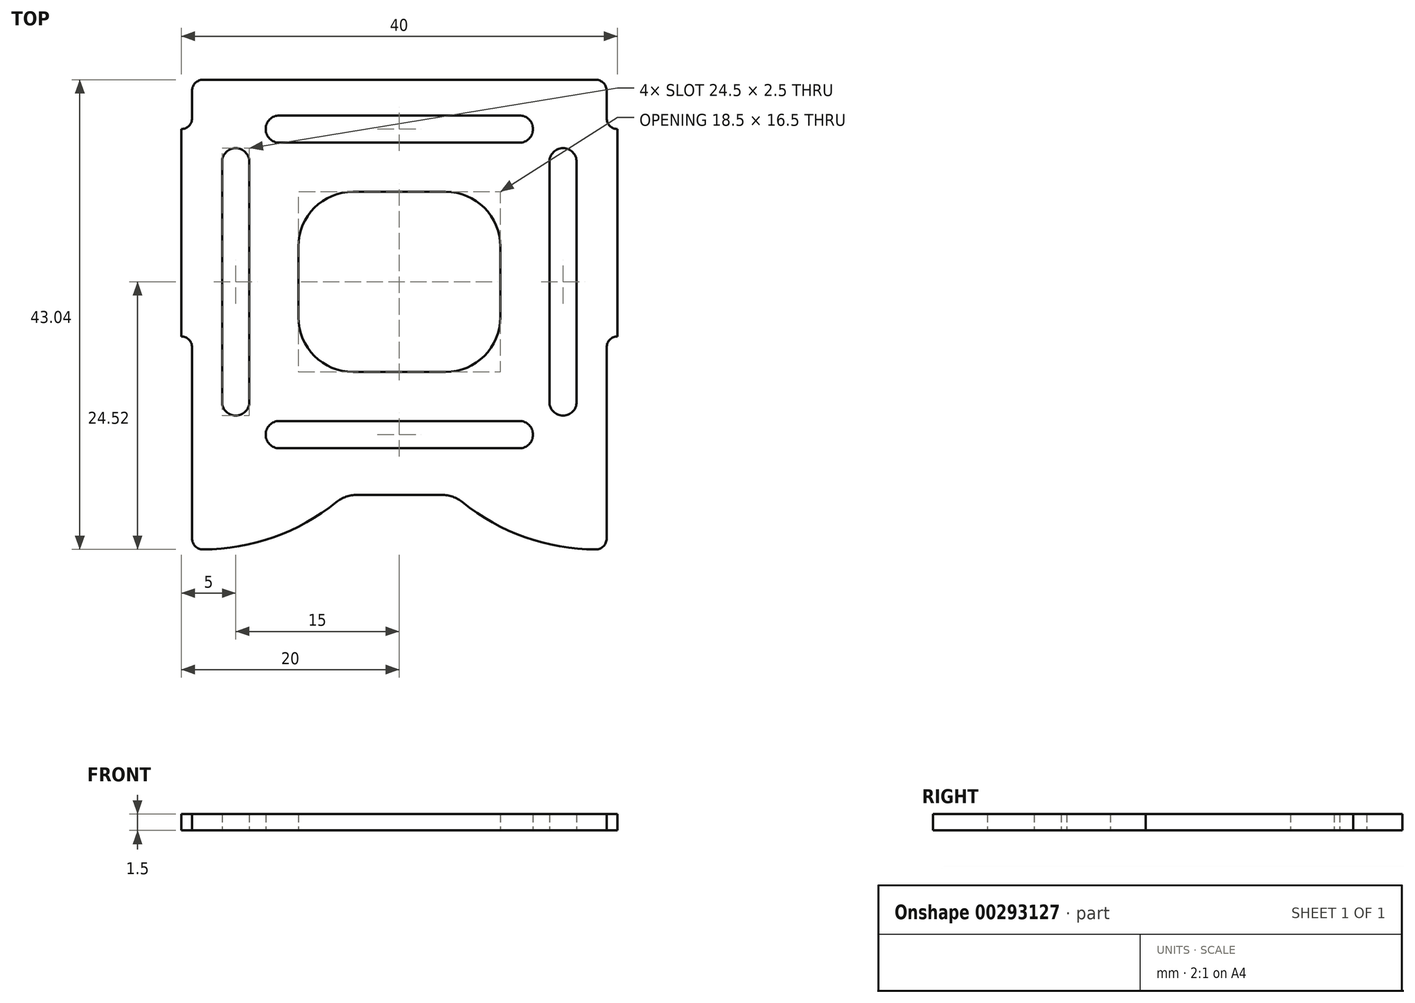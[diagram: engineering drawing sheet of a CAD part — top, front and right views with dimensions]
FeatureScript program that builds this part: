
annotation { "Feature Type Name" : "Feature", "Feature Type Description" : "" }
export const myFeature = defineFeature(function(context is Context, id is Id, definition is map)
    precondition{}
    {
        {
            var Q0;
            Q0=qCreatedBy(makeId("Top.planeOp"),FACE);
            var sketch = newSketch(context, id + "F0", { "sketchPlane" : qUnion([Q0])});
            skArc(sketch, "E0", {"start": v(-20, 17) * mm, "mid": v(-19.3, 17.3) * mm, "end": v(-19, 18) * mm});
            skLineSegment(sketch, "E1", {"start": v(-19, 18) * mm, "end": v(-19, 20.52) * mm});
            skArc(sketch, "E2", {"start": v(-18, 21.52) * mm, "mid": v(-18.7, 21.23) * mm, "end": v(-19, 20.52) * mm});
            skLineSegment(sketch, "E3", {"start": v(-18, 21.52) * mm, "end": v(18, 21.52) * mm});
            skArc(sketch, "E4", {"start": v(19, 20.52) * mm, "mid": v(18.7, 21.23) * mm, "end": v(18, 21.52) * mm});
            skLineSegment(sketch, "E5", {"start": v(19, 20.52) * mm, "end": v(19, 18) * mm});
            skArc(sketch, "E6", {"start": v(19, 18) * mm, "mid": v(19.3, 17.3) * mm, "end": v(20, 17) * mm});
            skLineSegment(sketch, "E7", {"start": v(20, 17) * mm, "end": v(20, -2) * mm});
            skArc(sketch, "E8", {"start": v(20, -2) * mm, "mid": v(19.3, -2.3) * mm, "end": v(19, -3) * mm});
            skLineSegment(sketch, "E9", {"start": v(19, -3) * mm, "end": v(19, -20.52) * mm});
            skArc(sketch, "E10", {"start": v(18, -21.52) * mm, "mid": v(18.7, -21.23) * mm, "end": v(19, -20.52) * mm});
            skArc(sketch, "E11", {"start": v(-19, -20.52) * mm, "mid": v(-18.7, -21.23) * mm, "end": v(-18, -21.52) * mm});
            skLineSegment(sketch, "E12", {"start": v(-19, -20.52) * mm, "end": v(-19, -3) * mm});
            skArc(sketch, "E13", {"start": v(-19, -3) * mm, "mid": v(-19.3, -2.3) * mm, "end": v(-20, -2) * mm});
            skLineSegment(sketch, "E14", {"start": v(-20, -2) * mm, "end": v(-20, 17) * mm});
            skLineSegment(sketch, "E15", {"start": v(-4.25, -5.25) * mm, "end": v(4.25, -5.25) * mm});
            skArc(sketch, "E16", {"start": v(-9.25, -0.25) * mm, "mid": v(-7.79, -3.79) * mm, "end": v(-4.25, -5.25) * mm});
            skLineSegment(sketch, "E17", {"start": v(-9.25, 6.25) * mm, "end": v(-9.25, -0.25) * mm});
            skArc(sketch, "E18", {"start": v(-4.25, 11.25) * mm, "mid": v(-7.79, 9.79) * mm, "end": v(-9.25, 6.25) * mm});
            skLineSegment(sketch, "E19", {"start": v(4.25, 11.25) * mm, "end": v(-4.25, 11.25) * mm});
            skArc(sketch, "E20", {"start": v(9.25, 6.25) * mm, "mid": v(7.79, 9.79) * mm, "end": v(4.25, 11.25) * mm});
            skLineSegment(sketch, "E21", {"start": v(9.25, -0.25) * mm, "end": v(9.25, 6.25) * mm});
            skArc(sketch, "E22", {"start": v(4.25, -5.25) * mm, "mid": v(7.79, -3.79) * mm, "end": v(9.25, -0.25) * mm});
            skLineSegment(sketch, "E23", {"start": v(11, -9.75) * mm, "end": v(-11, -9.75) * mm});
            skArc(sketch, "E24", {"start": v(11, -12.25) * mm, "mid": v(12.25, -11) * mm, "end": v(11, -9.75) * mm});
            skLineSegment(sketch, "E25", {"start": v(-11, -12.25) * mm, "end": v(11, -12.25) * mm});
            skArc(sketch, "E26", {"start": v(-11, -9.75) * mm, "mid": v(-12.25, -11) * mm, "end": v(-11, -12.25) * mm});
            skArc(sketch, "E27", {"start": v(16.25, 14) * mm, "mid": v(15, 15.25) * mm, "end": v(13.75, 14) * mm});
            skLineSegment(sketch, "E28", {"start": v(16.25, -8) * mm, "end": v(16.25, 14) * mm});
            skArc(sketch, "E29", {"start": v(13.75, -8) * mm, "mid": v(15, -9.25) * mm, "end": v(16.25, -8) * mm});
            skLineSegment(sketch, "E30", {"start": v(13.75, 14) * mm, "end": v(13.75, -8) * mm});
            skLineSegment(sketch, "E31", {"start": v(11, 18.25) * mm, "end": v(-11, 18.25) * mm});
            skArc(sketch, "E32", {"start": v(11, 15.75) * mm, "mid": v(12.25, 17) * mm, "end": v(11, 18.25) * mm});
            skLineSegment(sketch, "E33", {"start": v(-11, 15.75) * mm, "end": v(11, 15.75) * mm});
            skArc(sketch, "E34", {"start": v(-11, 18.25) * mm, "mid": v(-12.25, 17) * mm, "end": v(-11, 15.75) * mm});
            skLineSegment(sketch, "E35", {"start": v(-16.25, 14) * mm, "end": v(-16.25, -8) * mm});
            skArc(sketch, "E36", {"start": v(-13.75, 14) * mm, "mid": v(-15, 15.25) * mm, "end": v(-16.25, 14) * mm});
            skLineSegment(sketch, "E37", {"start": v(-13.75, -8) * mm, "end": v(-13.75, 14) * mm});
            skArc(sketch, "E38", {"start": v(-16.25, -8) * mm, "mid": v(-15, -9.25) * mm, "end": v(-13.75, -8) * mm});
            skArc(sketch, "E39", {"start": v(5.78, -17.2) * mm, "mid": v(11.52, -20.4) * mm, "end": v(18, -21.52) * mm});
            skArc(sketch, "E40", {"start": v(-18, -21.52) * mm, "mid": v(-11.52, -20.4) * mm, "end": v(-5.78, -17.2) * mm});
            skLineSegment(sketch, "E41", {"start": v(-3.9, -16.52) * mm, "end": v(3.9, -16.52) * mm});
            skArc(sketch, "E42", {"start": v(-3.9, -16.52) * mm, "mid": v(-4.9, -16.7) * mm, "end": v(-5.78, -17.2) * mm});
            skArc(sketch, "E43", {"start": v(5.78, -17.2) * mm, "mid": v(4.9, -16.7) * mm, "end": v(3.9, -16.52) * mm});
            skSolve(sketch);
        }
        {
            var Q0;
            Q0 = qSketchRegion(id + "F0", true);
            extrude(context, id + "F1", {"entities" : qUnion([Q0]), "depth" : 1.5 * mm});
        }
    });
